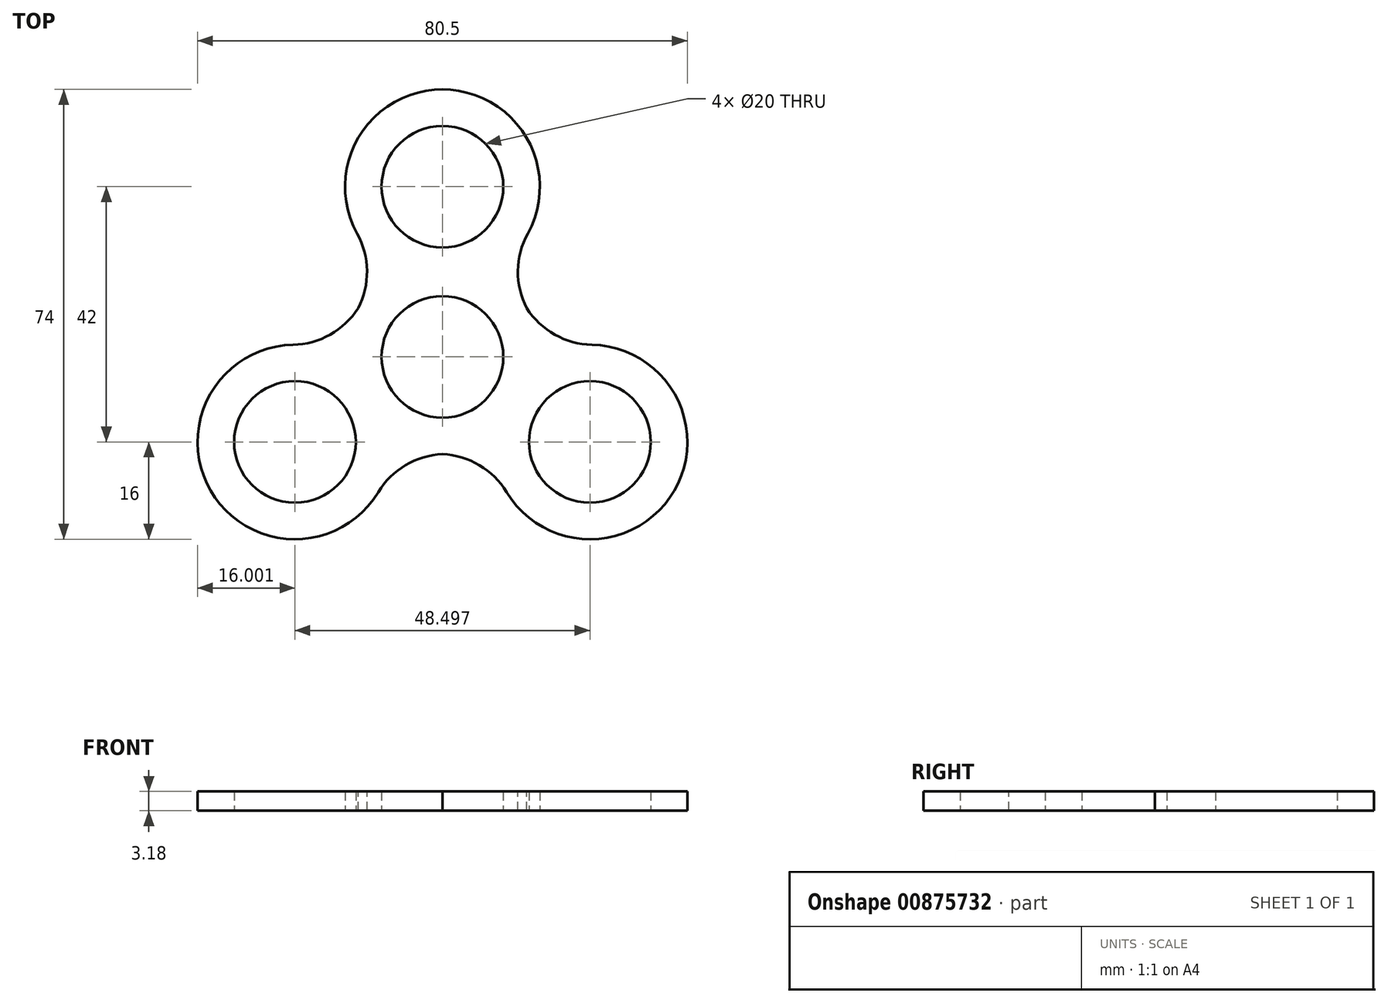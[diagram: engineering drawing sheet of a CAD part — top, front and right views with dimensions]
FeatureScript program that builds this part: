
annotation { "Feature Type Name" : "Feature", "Feature Type Description" : "" }
export const myFeature = defineFeature(function(context is Context, id is Id, definition is map)
    precondition{}
    {
        {
            assignVariable(context, id + "F0", {"name" : "thick", "anyValue" : 3.17 * mm});
        }
        {
            assignVariable(context, id + "F1", {"name" : "filletrad", "anyValue" : 13 * mm});
        }
        {
            var Q0;
            Q0=qCreatedBy(makeId("Top.planeOp"),FACE);
            var sketch = newSketch(context, id + "F2", { "sketchPlane" : qUnion([Q0])});
            skLineSegment(sketch, "E0", {"start": v(0, 0) * mm, "end": v(0, 28) * mm, "construction": true});
            skCircle(sketch, "E1", {"center": v(0, 28) * mm, "radius": 16 * mm});
            skCircle(sketch, "E2", {"center": v(0, 28) * mm, "radius": 10 * mm});
            skCircle(sketch, "E3.1.0", {"center": v(-24.25, -14) * mm, "radius": 16 * mm});
            skCircle(sketch, "E3.1.1", {"center": v(-24.25, -14) * mm, "radius": 10 * mm});
            skCircle(sketch, "E3.2.0", {"center": v(24.25, -14) * mm, "radius": 16 * mm});
            skCircle(sketch, "E3.2.1", {"center": v(24.25, -14) * mm, "radius": 10 * mm});
            skPoint(sketch, "E3.center", {"position": v(0, 0) * mm});
            skCircle(sketch, "E4", {"center": v(0, 0) * mm, "radius": 10 * mm});
            skCircle(sketch, "E5", {"center": v(0, 0) * mm, "radius": 16 * mm});
            skSolve(sketch);
        }
        {
            var Q0;
            Q0=makeQuery(id+"F2.imprint","IMPRINT",FACE,{"disambiguationData":[TD([[makeQuery(id+"F2.imprint","IMPRINT",EDGE,{"derivedFrom":sQuery(id+"F2.wireOp",EDGE,"E2")}),-1.0]])]});
            var Q1;
            Q1=makeQuery(id+"F2.imprint","IMPRINT",FACE,{"disambiguationData":[TD([[makeQuery(id+"F2.imprint","IMPRINT",EDGE,{"derivedFrom":sQuery(id+"F2.wireOp",EDGE,"E4")}),-1.0]])]});
            var Q2;
            Q2=makeQuery(id+"F2.imprint","IMPRINT",FACE,{"disambiguationData":[TD([[makeQuery(id+"F2.imprint","IMPRINT",EDGE,{"derivedFrom":sQuery(id+"F2.wireOp",EDGE,"E3.1.1")}),-1.0]])]});
            var Q3;
            {var subQ0=sQuery(id+"F2.wireOp",EDGE,"E5");var subQ1=sQuery(id+"F2.wireOp",EDGE,"E3.1.0");var subQ2=makeQuery(id+"F2.imprint","INTERSECT",VERTEX,{"disambiguationData":[OD(0.0)],"derivedFrom":[subQ1,subQ0]});Q3=makeQuery(id+"F2.imprint","IMPRINT",FACE,{"disambiguationData":[TD([[makeQuery(id+"F2.imprint","IMPRINT",EDGE,{"disambiguationData":[TD([[subQ2,1.0]])],"derivedFrom":subQ1}),1.0]])]});}
            var Q4;
            {var subQ0=sQuery(id+"F2.wireOp",EDGE,"E5");var subQ1=sQuery(id+"F2.wireOp",EDGE,"E1");var subQ2=makeQuery(id+"F2.imprint","INTERSECT",VERTEX,{"disambiguationData":[OD(0.0)],"derivedFrom":[subQ1,subQ0]});Q4=makeQuery(id+"F2.imprint","IMPRINT",FACE,{"disambiguationData":[TD([[makeQuery(id+"F2.imprint","IMPRINT",EDGE,{"disambiguationData":[TD([[subQ2,-1.0]])],"derivedFrom":subQ1}),1.0]])]});}
            var Q5;
            {var subQ0=sQuery(id+"F2.wireOp",EDGE,"E5");var subQ1=sQuery(id+"F2.wireOp",EDGE,"E3.2.0");var subQ2=makeQuery(id+"F2.imprint","INTERSECT",VERTEX,{"disambiguationData":[OD(0.0)],"derivedFrom":[subQ1,subQ0]});Q5=makeQuery(id+"F2.imprint","IMPRINT",FACE,{"disambiguationData":[TD([[makeQuery(id+"F2.imprint","IMPRINT",EDGE,{"disambiguationData":[TD([[subQ2,1.0]])],"derivedFrom":subQ1}),1.0]])]});}
            var Q6;
            Q6=makeQuery(id+"F2.imprint","IMPRINT",FACE,{"disambiguationData":[TD([[makeQuery(id+"F2.imprint","IMPRINT",EDGE,{"derivedFrom":sQuery(id+"F2.wireOp",EDGE,"E3.2.1")}),-1.0]])]});
            extrude(context, id + "F3", {"entities" : qUnion([Q0, Q1, Q2, Q3, Q4, Q5, Q6]), "endBound" : BoundingType.SYMMETRIC, "depth" : getVariable(context, 'thick'), "offsetDistance" : 25 * mm});
        }
        {
            var Q0;
            {var subQ0=sQuery(id+"F2.wireOp",EDGE,"E5");var subQ1=sQuery(id+"F2.wireOp",EDGE,"E1");Q0=makeQuery(id+"F3.opExtrude","SWEPT_EDGE",EDGE,{"disambiguationData":[OSD([subQ1,subQ0]),TDD([makeQuery(id+"F2.imprint","INTERSECT",VERTEX,{"disambiguationData":[OD(1.0)],"derivedFrom":[subQ1,subQ0]})])]});}
            var Q1;
            {var subQ0=sQuery(id+"F2.wireOp",EDGE,"E5");var subQ1=sQuery(id+"F2.wireOp",EDGE,"E3.2.0");Q1=makeQuery(id+"F3.opExtrude","SWEPT_EDGE",EDGE,{"disambiguationData":[OSD([subQ1,subQ0]),TDD([makeQuery(id+"F2.imprint","INTERSECT",VERTEX,{"disambiguationData":[OD(1.0)],"derivedFrom":[subQ1,subQ0]})])]});}
            var Q2;
            {var subQ0=sQuery(id+"F2.wireOp",EDGE,"E5");var subQ1=sQuery(id+"F2.wireOp",EDGE,"E3.2.0");Q2=makeQuery(id+"F3.opExtrude","SWEPT_EDGE",EDGE,{"disambiguationData":[OSD([subQ1,subQ0]),TDD([makeQuery(id+"F2.imprint","INTERSECT",VERTEX,{"disambiguationData":[OD(0.0)],"derivedFrom":[subQ1,subQ0]})])]});}
            var Q3;
            {var subQ0=sQuery(id+"F2.wireOp",EDGE,"E5");var subQ1=sQuery(id+"F2.wireOp",EDGE,"E3.1.0");Q3=makeQuery(id+"F3.opExtrude","SWEPT_EDGE",EDGE,{"disambiguationData":[OSD([subQ1,subQ0]),TDD([makeQuery(id+"F2.imprint","INTERSECT",VERTEX,{"disambiguationData":[OD(1.0)],"derivedFrom":[subQ1,subQ0]})])]});}
            var Q4;
            {var subQ0=sQuery(id+"F2.wireOp",EDGE,"E5");var subQ1=sQuery(id+"F2.wireOp",EDGE,"E3.1.0");Q4=makeQuery(id+"F3.opExtrude","SWEPT_EDGE",EDGE,{"disambiguationData":[OSD([subQ1,subQ0]),TDD([makeQuery(id+"F2.imprint","INTERSECT",VERTEX,{"disambiguationData":[OD(0.0)],"derivedFrom":[subQ1,subQ0]})])]});}
            var Q5;
            {var subQ0=sQuery(id+"F2.wireOp",EDGE,"E5");var subQ1=sQuery(id+"F2.wireOp",EDGE,"E1");Q5=makeQuery(id+"F3.opExtrude","SWEPT_EDGE",EDGE,{"disambiguationData":[OSD([subQ1,subQ0]),TDD([makeQuery(id+"F2.imprint","INTERSECT",VERTEX,{"disambiguationData":[OD(0.0)],"derivedFrom":[subQ1,subQ0]})])]});}
            fillet(context, id + "F4", {"entities" : qUnion([Q0, Q1, Q2, Q3, Q4, Q5]), "radius" : getVariable(context, 'filletrad'), "tangentPropagation" : true, "allowEdgeOverflow" : false});
        }
    });
